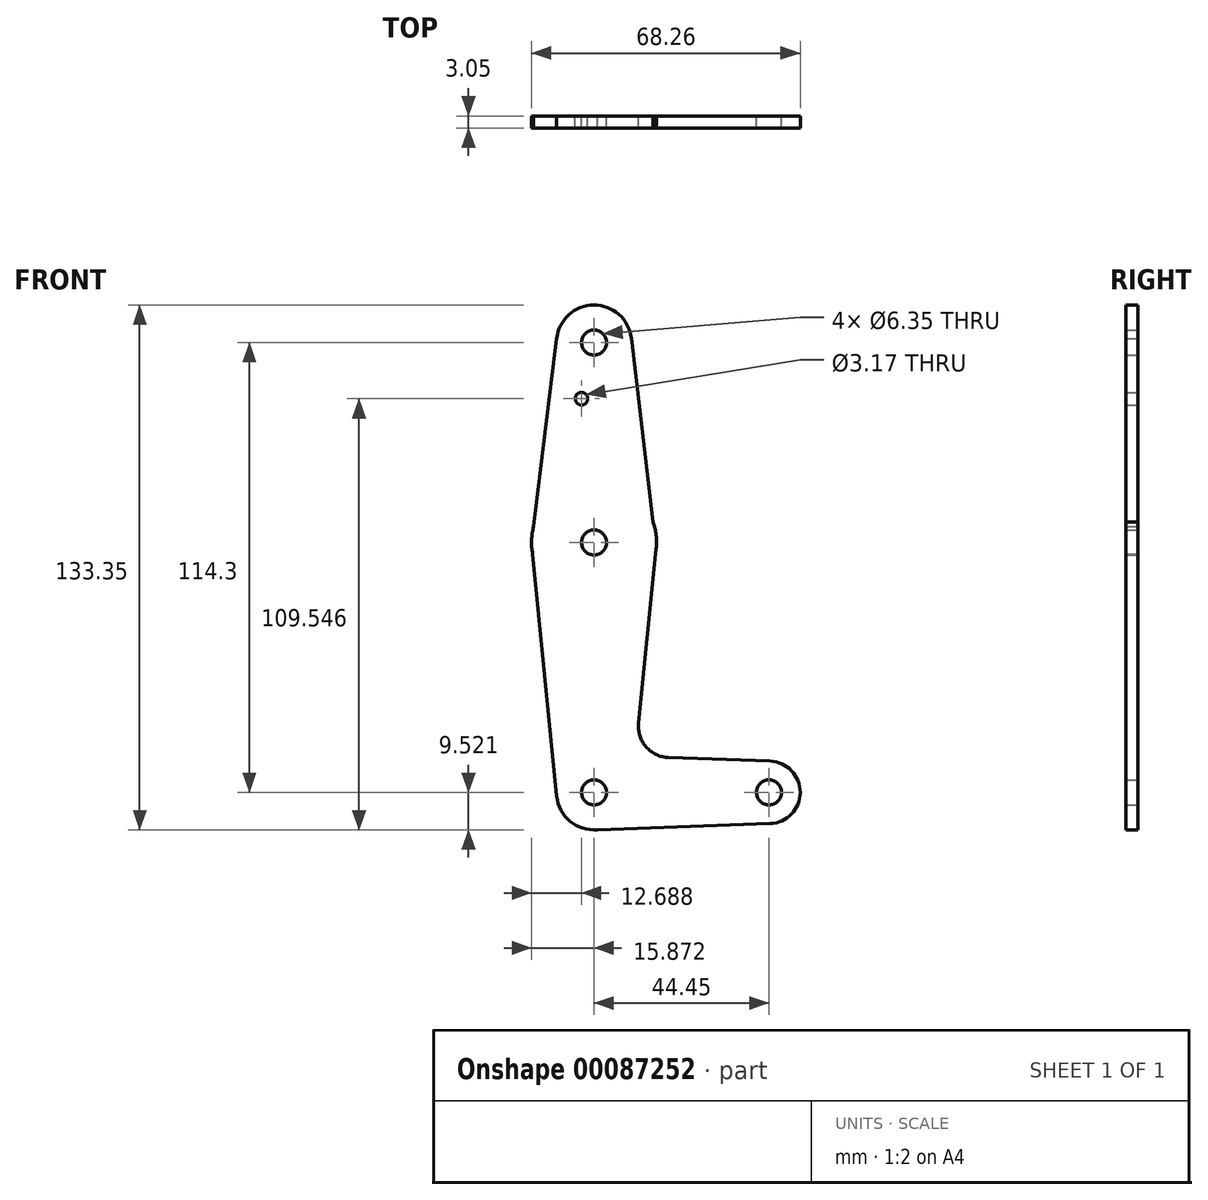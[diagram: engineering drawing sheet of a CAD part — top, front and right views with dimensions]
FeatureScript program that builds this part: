
annotation { "Feature Type Name" : "Feature", "Feature Type Description" : "" }
export const myFeature = defineFeature(function(context is Context, id is Id, definition is map)
    precondition{}
    {
        {
            var Q0;
            Q0=qCreatedBy(makeId("Front.planeOp"),FACE);
            var sketch = newSketch(context, id + "F0", { "sketchPlane" : qUnion([Q0])});
            skLineSegment(sketch, "E0", {"start": v(-30.72, -50.97) * mm, "end": v(13.73, -50.97) * mm, "construction": true});
            skLineSegment(sketch, "E1", {"start": v(-30.72, -50.97) * mm, "end": v(-30.72, 63.33) * mm, "construction": true});
            skCircle(sketch, "E2", {"center": v(-30.72, 12.53) * mm, "radius": 15.88 * mm});
            skCircle(sketch, "E3", {"center": v(-30.72, 63.33) * mm, "radius": 9.53 * mm});
            skCircle(sketch, "E4", {"center": v(-30.72, -50.97) * mm, "radius": 9.53 * mm});
            skCircle(sketch, "E5", {"center": v(13.73, -50.97) * mm, "radius": 7.94 * mm});
            skLineSegment(sketch, "E6", {"start": v(-40.2, 64.31) * mm, "end": v(-46.6, 12.31) * mm});
            skLineSegment(sketch, "E7", {"start": v(-46.6, 12.31) * mm, "end": v(-40.2, -51.91) * mm});
            skLineSegment(sketch, "E8", {"start": v(-30.9, -60.5) * mm, "end": v(14.01, -58.9) * mm});
            skLineSegment(sketch, "E9", {"start": v(-11.78, -42.12) * mm, "end": v(14.01, -43.04) * mm});
            skLineSegment(sketch, "E10", {"start": v(-19.41, -33.37) * mm, "end": v(-14.92, 10.93) * mm});
            skLineSegment(sketch, "E11", {"start": v(-14.92, 10.93) * mm, "end": v(-21.26, 64.45) * mm});
            skArc(sketch, "E12.filletArc", {"start": v(-19.41, -33.37) * mm, "mid": v(-17.5, -39.4) * mm, "end": v(-11.78, -42.12) * mm});
            skCircle(sketch, "E13", {"center": v(-30.72, 63.33) * mm, "radius": 3.18 * mm});
            skCircle(sketch, "E14", {"center": v(-30.72, 12.53) * mm, "radius": 3.18 * mm});
            skCircle(sketch, "E15", {"center": v(-30.72, -50.97) * mm, "radius": 3.18 * mm});
            skCircle(sketch, "E16", {"center": v(13.73, -50.97) * mm, "radius": 3.18 * mm});
            skCircle(sketch, "E17", {"center": v(-33.9, 49.06) * mm, "radius": 1.59 * mm});
            skSolve(sketch);
        }
        {
            var Q0;
            Q0 = qSketchRegion(id + "F0", true);
            extrude(context, id + "F1", {"entities" : qUnion([Q0]), "depth" : 3.05 * mm});
        }
    });
